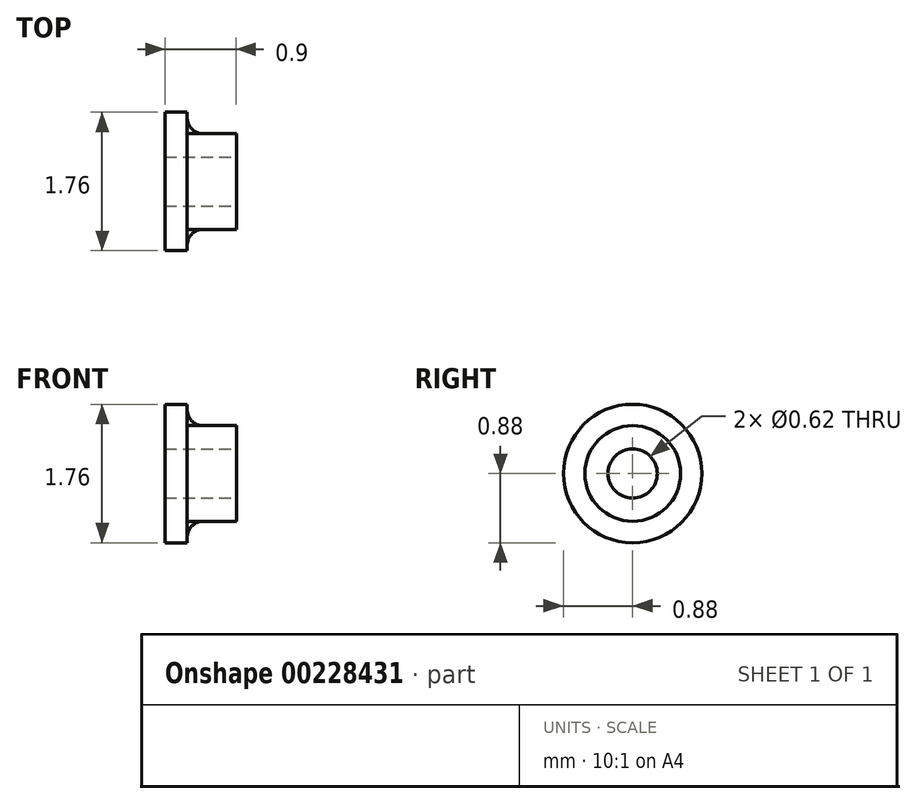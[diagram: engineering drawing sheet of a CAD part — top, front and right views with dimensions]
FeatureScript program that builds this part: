
annotation { "Feature Type Name" : "Feature", "Feature Type Description" : "" }
export const myFeature = defineFeature(function(context is Context, id is Id, definition is map)
    precondition{}
    {
        {
            var Q0;
            Q0=qCreatedBy(makeId("Top.planeOp"),FACE);
            var sketch = newSketch(context, id + "F0", { "sketchPlane" : qUnion([Q0])});
            skLineSegment(sketch, "E0", {"start": v(0.85, 0) * mm, "end": v(-0.38, 0) * mm});
            skLineSegment(sketch, "E1.bottom", {"start": v(-0.28, 0.88) * mm, "end": v(0, 0.88) * mm});
            skLineSegment(sketch, "E1.top", {"start": v(-0.28, 0.31) * mm, "end": v(0, 0.31) * mm});
            skLineSegment(sketch, "E1.left", {"start": v(-0.28, 0.88) * mm, "end": v(-0.28, 0.31) * mm});
            skLineSegment(sketch, "E1.right", {"start": v(0, 0.88) * mm, "end": v(0, 0.31) * mm});
            skLineSegment(sketch, "E2.bottom", {"start": v(0, 0.31) * mm, "end": v(0.62, 0.31) * mm});
            skLineSegment(sketch, "E2.top", {"start": v(0, 0.6) * mm, "end": v(0.62, 0.6) * mm});
            skLineSegment(sketch, "E2.left", {"start": v(0, 0.31) * mm, "end": v(0, 0.6) * mm});
            skLineSegment(sketch, "E2.right", {"start": v(0.62, 0.31) * mm, "end": v(0.62, 0.6) * mm});
            skLineSegment(sketch, "E3.MirrorCS", {"start": v(-0.28, -0.31) * mm, "end": v(0, -0.31) * mm});
            skLineSegment(sketch, "E4.MirrorCS", {"start": v(-0.28, -0.88) * mm, "end": v(-0.28, -0.31) * mm});
            skLineSegment(sketch, "E5.MirrorCS", {"start": v(0, -0.31) * mm, "end": v(0, -0.6) * mm});
            skLineSegment(sketch, "E6.MirrorCS", {"start": v(0, -0.88) * mm, "end": v(0, -0.31) * mm});
            skLineSegment(sketch, "E7.MirrorCS", {"start": v(-0.28, -0.88) * mm, "end": v(0, -0.88) * mm});
            skLineSegment(sketch, "E8.MirrorCS", {"start": v(0, -0.6) * mm, "end": v(0.62, -0.6) * mm});
            skLineSegment(sketch, "E9.MirrorCS", {"start": v(0.62, -0.31) * mm, "end": v(0.62, -0.6) * mm});
            skLineSegment(sketch, "E10.MirrorCS", {"start": v(0, -0.31) * mm, "end": v(0.62, -0.31) * mm});
            skSolve(sketch);
        }
        {
            var Q0;
            Q0=makeQuery(id+"F0.imprint","IMPRINT",FACE,{"disambiguationData":[TD([[makeQuery(id+"F0.imprint","IMPRINT",EDGE,{"derivedFrom":sQuery(id+"F0.wireOp",EDGE,"E2.bottom")}),1.0]])]});
            var Q1;
            Q1=makeQuery(id+"F0.imprint","IMPRINT",FACE,{"disambiguationData":[TD([[makeQuery(id+"F0.imprint","IMPRINT",EDGE,{"derivedFrom":sQuery(id+"F0.wireOp",EDGE,"E1.bottom")}),-1.0]])]});
            var Q2;
            Q2=makeQuery(id+"F0.imprint","IMPRINT",FACE,{"disambiguationData":[TD([[makeQuery(id+"F0.imprint","IMPRINT",EDGE,{"derivedFrom":sQuery(id+"F0.wireOp",EDGE,"E4.MirrorCS")}),-1.0]])]});
            var Q3;
            {var subQ2=sQuery(id+"F0.wireOp",EDGE,"E8.MirrorCS");Q3=makeQuery(id+"F0.imprint","IMPRINT",FACE,{"disambiguationData":[TD([[makeQuery(id+"F0.imprint","IMPRINT",EDGE,{"derivedFrom":subQ2}),1.0]])]});}
            var Q4;
            Q4=sQuery(id+"F0.wireOp",EDGE,"E0");
            revolve(context, id + "F1", {"entities" : qUnion([Q0, Q1, Q2, Q3]), "axis" : qUnion([Q4]), "revolveType" : RevolveType.FULL});
        }
        {
            var Q0;
            Q0=makeQuery(id+"F1.opRevolve","SWEPT_EDGE",EDGE,{"disambiguationData":[OSD([sQuery(id+"F0.wireOp",EDGE,"E6.MirrorCS"),sQuery(id+"F0.wireOp",EDGE,"E8.MirrorCS")])]});
            fillet(context, id + "F2", {"entities" : qUnion([Q0]), "radius" : .2 * mm, "tangentPropagation" : true, "allowEdgeOverflow" : false});
        }
    });
